# Revit family: Sanitary_Taps-Mixers_AXOR_46141007-AXOR-Edge-Thermostat-for-3-func_
name_source: partatom
category: Plumbing Fixtures
revit_build: Autodesk Revit 2015 (Build: 20140903_1530(x64)
units: mm (PartAtom-declared; Revit-internal decimal feet)

## types (1)
- Chrome 000
    BIMobject category = Taps & Mixers
    BIMobject category code = sanitary-taps-mixers
    BIMobject main category = Sanitary
    BIMobject main category code = sanitary
    BOSUseNativeGeometries = 1
    Brand url = https://www.axor-design.com
    Default Elevation = 4' - 0"
    Design country = Germany
    Edition number = 1
    IFC Classification = Sanitary Terminal
    Installation instructions = https://pro.hansgrohe-int.com
    Manufacturer country = Germany
    Manufacturer name = AXOR
    Masterformat 2014 Code = 22 41 39
    Masterformat 2014 Description = Residential Faucets, Supplies, and Trim
    Material main = Chrome
    NBS Reference Code = 35-06-82
    NBS Reference Description = Shower Mixers
    OmniClass Code = 23-31 15 11
    OmniClass Description = Bath Shower Units
    Product Guid = f87c6660-6236-4159-9954-838e724c8311
    Product SKU = 46141007
    Product data url = https://bimobject.com
    Product family = AXOR Edge
    Product group = Shower thermostat
    Product name = 46141007 AXOR Edge Thermostat for 3 functions for exposed/concealed installation - diamond cut
    Product url = https://pro.hansgrohe-int.com
    QR code = http://bimobject.com
    Technical description = https://pro.hansgrohe-int.com
    UNSPSC Code = 30181503
    Uniclass 1.4 Code = L721
    Uniclass 1.4 Description = Sanitary equipment
    Uniclass 2.0 Code = PR-35-06-82
    Uniclass 2.0 Description = Shower Mixers
    Uniclass 2015 Code = Pr_40_20_87_81
    Uniclass 2015 Name = Shower thermostatic water supply sets
    Uniformat II Code = D2010
    Uniformat II Description = Plumbing Fixtures

## geometry (parser evidence)
native form markers: Sweep x3
no freeform markers — native parametric forms only
